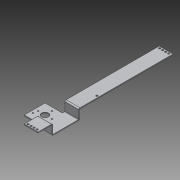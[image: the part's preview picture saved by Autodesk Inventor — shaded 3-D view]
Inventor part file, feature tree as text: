
AUTODESK INVENTOR PART (.ipt)
format: ipt  version: 2014 SP1 (Build 180222100, 222)  size: 300,032 bytes
history: native  units: in
note: dims shown in document units (in); Inventor stores cm internally (conversion verified against a paired STEP export)
features: reference x9, sheet_metal_op x7, other x6, sketch x5, projected_geometry x1
ambient origin geometry x8: Origin, YZ Plane, XZ Plane, XY Plane, X Axis, Y Axis, Z Axis, Center Point
bodies: Solid1 (feature_tree)
feature tree (28):
  sheet_metal_op  "Face1"
  sheet_metal_op  "Flange1"
  sheet_metal_op  "Flange2"
  sheet_metal_op  "Flange3"
  sketch  "Sketch1"  dims[d0=1.0in]
  other  "Plate1"
  sketch  "Sketch2"  dims[d1=1.0in]
  other  "Plate2"
  sheet_metal_op  "Bend1"
  sketch  "Sketch3"  dims[d2=1.0in]
  other  "Plate3"
  sheet_metal_op  "Bend2"
  sketch  "Sketch4"  dims[d3=0.5in]
  other  "Plate4"
  sheet_metal_op  "Bend3"
  sketch  "Sketch5"  dims[d4=2.0in d5=2.0in d6=0.5in d7=2.0in d8=0.125in d9=0.125in d10=0.0625in d11=0.25in d12=0.125in d13=1.5in d14=90.0deg d15=0.05in d16=0.5in d17=0.125in d18=0.125in d19=0.125in d20=0.0625in d21=0.25in d22=0.125in d23=2.125in d24=90.0deg d25=0.05in d26=0.5in d27=0.125in d28=0.125in d29=0.125in d30=0.0625in d31=0.25in d32=0.125in d33=13.625in d34=90.0deg d35=0.05in d36=0.5in d37=0.125in d38=0.125in d39=0.125in d40=0.0in d41=0.2in d42=0.375in d43=0.875in]
  projected_geometry  "Projected Loop1"
  reference  "Reference1"
  reference  "Reference2"
  reference  "Reference3"
  reference  "Reference4"
  reference  "Reference5"
  reference  "Reference6"
  reference  "Reference7"
  reference  "Reference8"
  reference  "Reference9"
  other  "Cut1"
  other  "Definition1"
